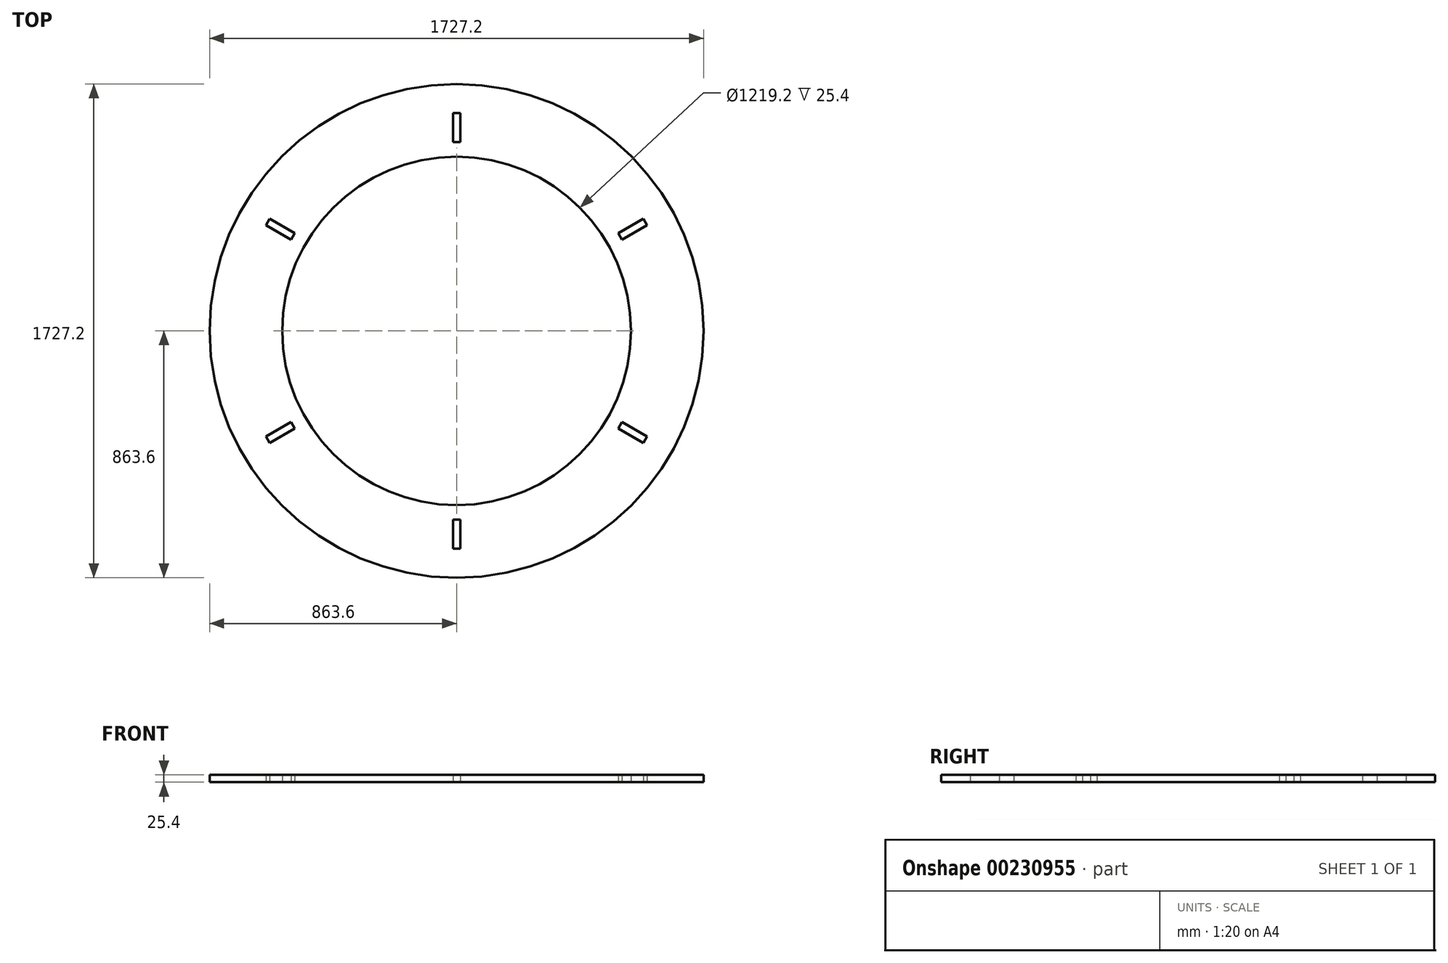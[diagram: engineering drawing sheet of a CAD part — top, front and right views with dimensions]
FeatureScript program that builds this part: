
annotation { "Feature Type Name" : "Feature", "Feature Type Description" : "" }
export const myFeature = defineFeature(function(context is Context, id is Id, definition is map)
    precondition{}
    {
        {
            var Q0;
            Q0=qCreatedBy(makeId("Top.planeOp"),FACE);
            var sketch = newSketch(context, id + "F0", { "sketchPlane" : qUnion([Q0])});
            skCircle(sketch, "E0", {"center": v(0, 0) * mm, "radius": 609.6 * mm});
            skCircle(sketch, "E1", {"center": v(0, 0) * mm, "radius": 863.6 * mm});
            skLineSegment(sketch, "E2.bottom", {"start": v(12.7, 762) * mm, "end": v(-12.7, 762) * mm});
            skLineSegment(sketch, "E2.top", {"start": v(12.7, 660.4) * mm, "end": v(-12.7, 660.4) * mm});
            skLineSegment(sketch, "E2.left", {"start": v(12.7, 762) * mm, "end": v(12.7, 660.4) * mm});
            skLineSegment(sketch, "E2.right", {"start": v(-12.7, 762) * mm, "end": v(-12.7, 660.4) * mm});
            skPoint(sketch, "E2.middle", {"position": v(0, 711.2) * mm});
            skLineSegment(sketch, "E3.1.0", {"start": v(-653.56, 392) * mm, "end": v(-565.57, 341.2) * mm});
            skLineSegment(sketch, "E3.1.1", {"start": v(-666.26, 370) * mm, "end": v(-578.27, 319.2) * mm});
            skLineSegment(sketch, "E3.1.2", {"start": v(-653.56, 392) * mm, "end": v(-666.26, 370) * mm});
            skLineSegment(sketch, "E3.1.3", {"start": v(-565.57, 341.2) * mm, "end": v(-578.27, 319.2) * mm});
            skLineSegment(sketch, "E3.2.0", {"start": v(-666.26, -370) * mm, "end": v(-578.27, -319.2) * mm});
            skLineSegment(sketch, "E3.2.1", {"start": v(-653.56, -392) * mm, "end": v(-565.57, -341.2) * mm});
            skLineSegment(sketch, "E3.2.2", {"start": v(-666.26, -370) * mm, "end": v(-653.56, -392) * mm});
            skLineSegment(sketch, "E3.2.3", {"start": v(-578.27, -319.2) * mm, "end": v(-565.57, -341.2) * mm});
            skLineSegment(sketch, "E3.3.0", {"start": v(-12.7, -762) * mm, "end": v(-12.7, -660.4) * mm});
            skLineSegment(sketch, "E3.3.1", {"start": v(12.7, -762) * mm, "end": v(12.7, -660.4) * mm});
            skLineSegment(sketch, "E3.3.2", {"start": v(-12.7, -762) * mm, "end": v(12.7, -762) * mm});
            skLineSegment(sketch, "E3.3.3", {"start": v(-12.7, -660.4) * mm, "end": v(12.7, -660.4) * mm});
            skLineSegment(sketch, "E3.4.0", {"start": v(653.56, -392) * mm, "end": v(565.57, -341.2) * mm});
            skLineSegment(sketch, "E3.4.1", {"start": v(666.26, -370) * mm, "end": v(578.27, -319.2) * mm});
            skLineSegment(sketch, "E3.4.2", {"start": v(653.56, -392) * mm, "end": v(666.26, -370) * mm});
            skLineSegment(sketch, "E3.4.3", {"start": v(565.57, -341.2) * mm, "end": v(578.27, -319.2) * mm});
            skLineSegment(sketch, "E3.5.0", {"start": v(666.26, 370) * mm, "end": v(578.27, 319.2) * mm});
            skLineSegment(sketch, "E3.5.1", {"start": v(653.56, 392) * mm, "end": v(565.57, 341.2) * mm});
            skLineSegment(sketch, "E3.5.2", {"start": v(666.26, 370) * mm, "end": v(653.56, 392) * mm});
            skLineSegment(sketch, "E3.5.3", {"start": v(578.27, 319.2) * mm, "end": v(565.57, 341.2) * mm});
            skSolve(sketch);
        }
        {
            var Q0;
            Q0=qSketchRegion(id+"F0",true);
            extrude(context, id + "F1", {"entities" : qUnion([Q0]), "depth" : 25.4 * mm});
        }
    });
